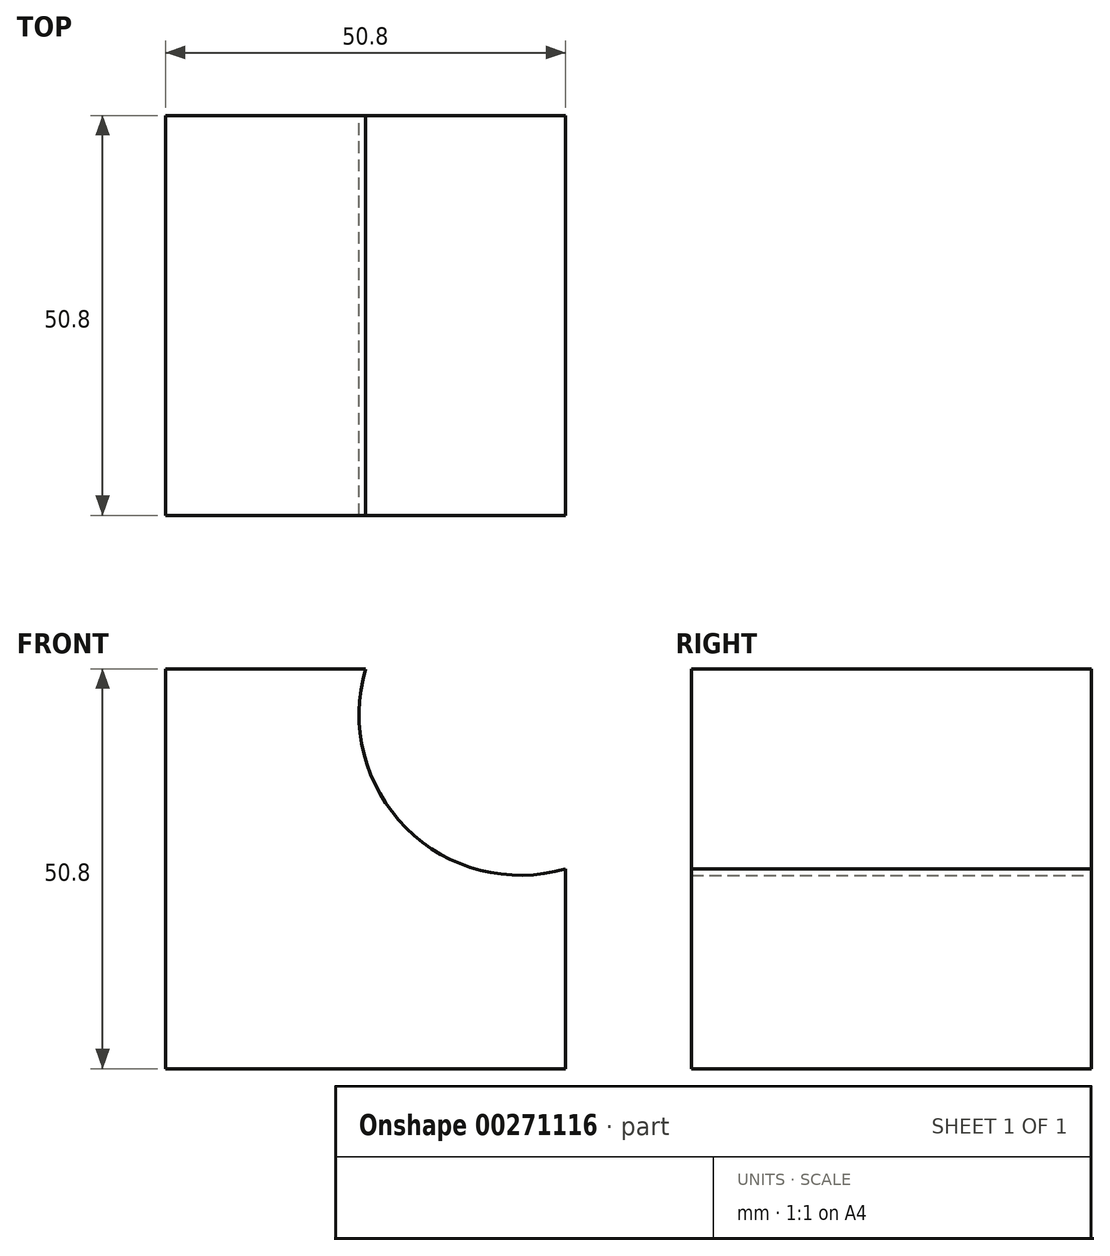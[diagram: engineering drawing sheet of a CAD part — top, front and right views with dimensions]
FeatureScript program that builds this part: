
annotation { "Feature Type Name" : "Feature", "Feature Type Description" : "" }
export const myFeature = defineFeature(function(context is Context, id is Id, definition is map)
    precondition{}
    {
        {
            var Q0;
            Q0=qCreatedBy(makeId("Front.planeOp"),FACE);
            var sketch = newSketch(context, id + "F0", { "sketchPlane" : qUnion([Q0])});
            skLineSegment(sketch, "E0", {"start": v(0, 0) * mm, "end": v(-50.8, 0) * mm});
            skLineSegment(sketch, "E1", {"start": v(-50.8, 0) * mm, "end": v(-50.8, 50.8) * mm});
            skLineSegment(sketch, "E2", {"start": v(-50.8, 50.8) * mm, "end": v(-25.4, 50.8) * mm});
            skLineSegment(sketch, "E3", {"start": v(0, 0) * mm, "end": v(0, 25.4) * mm});
            skArc(sketch, "E4", {"start": v(-25.4, 50.8) * mm, "mid": v(-20.24, 30.56) * mm, "end": v(0, 25.4) * mm});
            skSolve(sketch);
        }
        {
            var Q0;
            Q0 = qSketchRegion(id + "F0", true);
            extrude(context, id + "F1", {"entities" : qUnion([Q0]), "depth" : 50.8 * mm});
        }
    });
